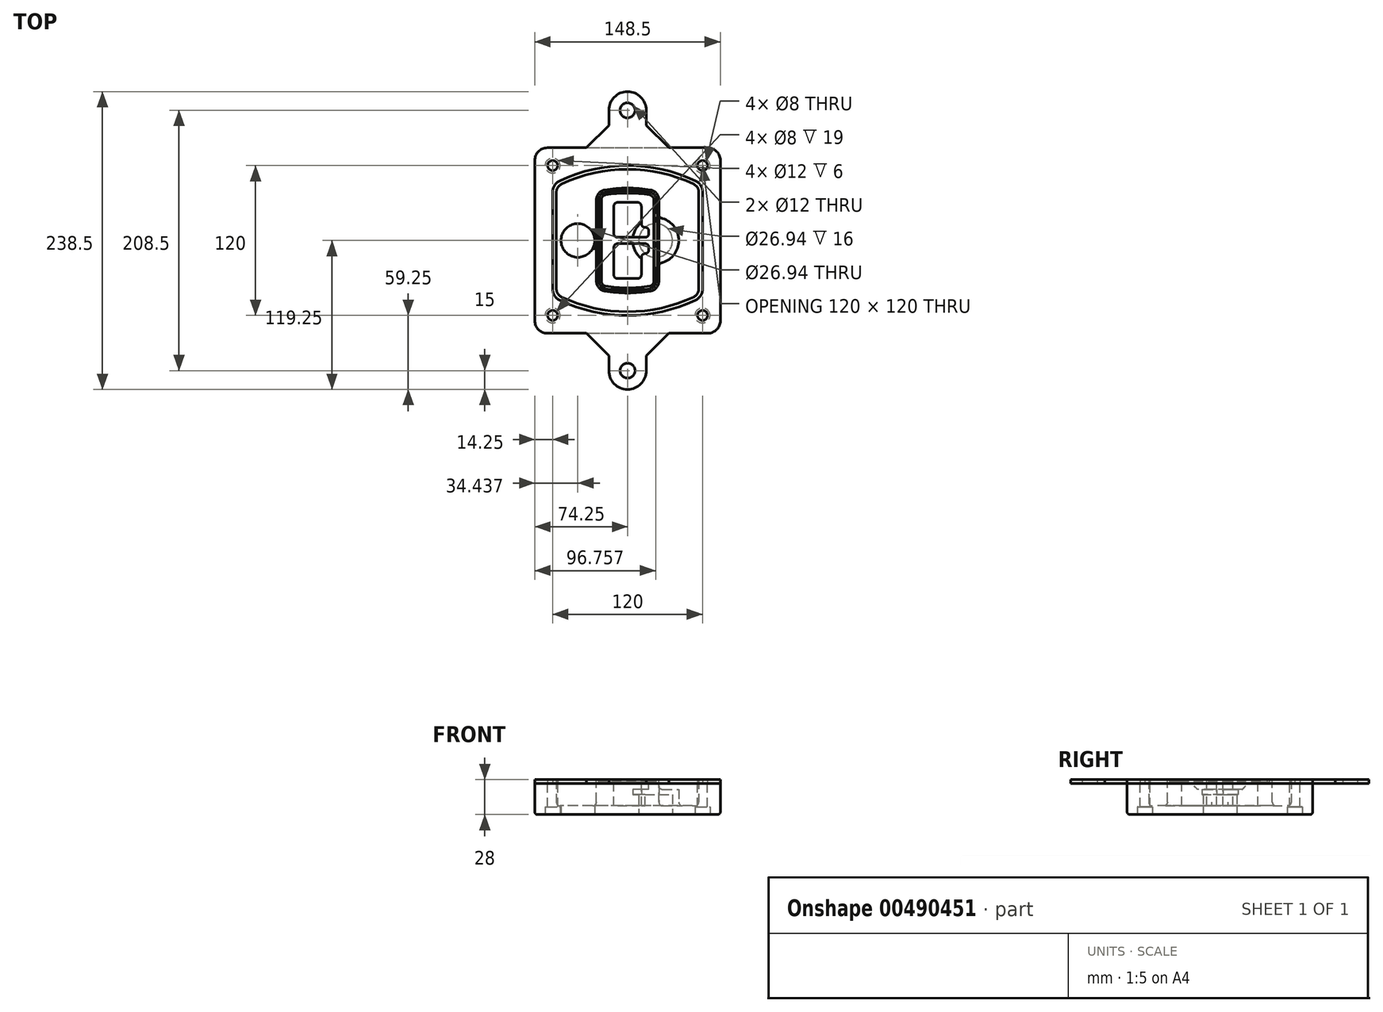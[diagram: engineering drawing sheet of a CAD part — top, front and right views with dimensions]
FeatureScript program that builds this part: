
annotation { "Feature Type Name" : "Feature", "Feature Type Description" : "" }
export const myFeature = defineFeature(function(context is Context, id is Id, definition is map)
    precondition{}
    {
        {
            var Q0;
            Q0=qCreatedBy(makeId("Top.planeOp"),FACE);
            var sketch = newSketch(context, id + "F0", { "sketchPlane" : qUnion([Q0])});
            skPoint(sketch, "E0.rect.middle", {"position": v(0, 0) * mm});
            skLineSegment(sketch, "E1.bottom", {"start": v(-64.25, -74.25) * mm, "end": v(64.25, -74.25) * mm});
            skLineSegment(sketch, "E1.top", {"start": v(-64.25, 74.25) * mm, "end": v(64.25, 74.25) * mm});
            skLineSegment(sketch, "E1.left", {"start": v(-74.25, -64.25) * mm, "end": v(-74.25, 64.25) * mm});
            skLineSegment(sketch, "E1.right", {"start": v(74.25, -64.25) * mm, "end": v(74.25, 64.25) * mm});
            skLineSegment(sketch, "E2", {"start": v(-74.25, 74.25) * mm, "end": v(74.25, -74.25) * mm, "construction": true});
            skLineSegment(sketch, "E3", {"start": v(74.25, 74.25) * mm, "end": v(-74.25, -74.25) * mm, "construction": true});
            skCircle(sketch, "E4", {"center": v(-60, 60) * mm, "radius": 4 * mm});
            skCircle(sketch, "E5", {"center": v(60, 60) * mm, "radius": 4 * mm});
            skCircle(sketch, "E6", {"center": v(60, -60) * mm, "radius": 4 * mm});
            skCircle(sketch, "E7", {"center": v(-60, -60) * mm, "radius": 4 * mm});
            skLineSegment(sketch, "E8", {"start": v(-60, 60) * mm, "end": v(60, 60) * mm, "construction": true});
            skLineSegment(sketch, "E9", {"start": v(60, 60) * mm, "end": v(60, -60) * mm, "construction": true});
            skLineSegment(sketch, "E10", {"start": v(60, -60) * mm, "end": v(-60, -60) * mm, "construction": true});
            skLineSegment(sketch, "E11", {"start": v(-60, -60) * mm, "end": v(-60, 60) * mm, "construction": true});
            skLineSegment(sketch, "E12", {"start": v(-60, 38.83) * mm, "end": v(-60, -38.83) * mm});
            skLineSegment(sketch, "E13", {"start": v(60, 38.83) * mm, "end": v(60, -38.83) * mm});
            skArc(sketch, "E14", {"start": v(54.26, 47.88) * mm, "mid": v(0, 60) * mm, "end": v(-54.26, 47.88) * mm});
            skArc(sketch, "E15", {"start": v(-54.26, -47.88) * mm, "mid": v(0, -60) * mm, "end": v(54.26, -47.88) * mm});
            skLineSegment(sketch, "E16", {"start": v(-60, 0) * mm, "end": v(60, 0) * mm, "construction": true});
            skPoint(sketch, "E17.visualSharp", {"position": v(-60, -45) * mm});
            skArc(sketch, "E17.filletArc", {"start": v(-60, -38.83) * mm, "mid": v(-58.44, -44.2) * mm, "end": v(-54.26, -47.88) * mm});
            skPoint(sketch, "E18.visualSharp", {"position": v(-60, 45) * mm});
            skArc(sketch, "E18.filletArc", {"start": v(-54.26, 47.88) * mm, "mid": v(-58.44, 44.2) * mm, "end": v(-60, 38.83) * mm});
            skPoint(sketch, "E19.visualSharp", {"position": v(60, 45) * mm});
            skArc(sketch, "E19.filletArc", {"start": v(60, 38.83) * mm, "mid": v(58.44, 44.2) * mm, "end": v(54.26, 47.88) * mm});
            skPoint(sketch, "E20.visualSharp", {"position": v(60, -45) * mm});
            skArc(sketch, "E20.filletArc", {"start": v(54.26, -47.88) * mm, "mid": v(58.44, -44.2) * mm, "end": v(60, -38.83) * mm});
            skPoint(sketch, "E21.visualSharp", {"position": v(-74.25, 74.25) * mm});
            skArc(sketch, "E21.filletArc", {"start": v(-64.25, 74.25) * mm, "mid": v(-71.32, 71.32) * mm, "end": v(-74.25, 64.25) * mm});
            skPoint(sketch, "E22.visualSharp", {"position": v(74.25, 74.25) * mm});
            skArc(sketch, "E22.filletArc", {"start": v(74.25, 64.25) * mm, "mid": v(71.32, 71.32) * mm, "end": v(64.25, 74.25) * mm});
            skPoint(sketch, "E23.visualSharp", {"position": v(74.25, -74.25) * mm});
            skArc(sketch, "E23.filletArc", {"start": v(64.25, -74.25) * mm, "mid": v(71.32, -71.32) * mm, "end": v(74.25, -64.25) * mm});
            skPoint(sketch, "E24.visualSharp", {"position": v(-74.25, -74.25) * mm});
            skArc(sketch, "E24.filletArc", {"start": v(-74.25, -64.25) * mm, "mid": v(-71.32, -71.32) * mm, "end": v(-64.25, -74.25) * mm});
            skArc(sketch, "E25.0", {"start": v(57, 38.83) * mm, "mid": v(55.9, 42.58) * mm, "end": v(52.98, 45.17) * mm});
            skLineSegment(sketch, "E25.1", {"start": v(57, 38.83) * mm, "end": v(57, -38.83) * mm});
            skArc(sketch, "E25.2", {"start": v(52.98, -45.17) * mm, "mid": v(55.9, -42.58) * mm, "end": v(57, -38.83) * mm});
            skArc(sketch, "E25.3", {"start": v(-52.98, -45.17) * mm, "mid": v(0, -57) * mm, "end": v(52.98, -45.17) * mm});
            skArc(sketch, "E25.4", {"start": v(-57, -38.83) * mm, "mid": v(-55.9, -42.58) * mm, "end": v(-52.98, -45.17) * mm});
            skArc(sketch, "E25.5", {"start": v(52.98, 45.17) * mm, "mid": v(0, 57) * mm, "end": v(-52.98, 45.17) * mm});
            skLineSegment(sketch, "E25.6", {"start": v(-57, 38.83) * mm, "end": v(-57, -38.83) * mm});
            skArc(sketch, "E25.7", {"start": v(-52.98, 45.17) * mm, "mid": v(-55.9, 42.58) * mm, "end": v(-57, 38.83) * mm});
            skArc(sketch, "E26.0", {"start": v(-55.96, 51.5) * mm, "mid": v(-61.82, 46.33) * mm, "end": v(-64, 38.83) * mm});
            skArc(sketch, "E26.1", {"start": v(55.96, 51.5) * mm, "mid": v(0, 64) * mm, "end": v(-55.96, 51.5) * mm});
            skArc(sketch, "E26.2", {"start": v(64, 38.83) * mm, "mid": v(61.82, 46.33) * mm, "end": v(55.96, 51.5) * mm});
            skLineSegment(sketch, "E26.3", {"start": v(64, 38.83) * mm, "end": v(64, -38.83) * mm});
            skArc(sketch, "E26.4", {"start": v(55.96, -51.5) * mm, "mid": v(61.82, -46.33) * mm, "end": v(64, -38.83) * mm});
            skLineSegment(sketch, "E26.5", {"start": v(-64, 38.83) * mm, "end": v(-64, -38.83) * mm});
            skArc(sketch, "E26.6", {"start": v(-55.96, -51.5) * mm, "mid": v(0, -64) * mm, "end": v(55.96, -51.5) * mm});
            skArc(sketch, "E26.7", {"start": v(-64, -38.83) * mm, "mid": v(-61.82, -46.33) * mm, "end": v(-55.96, -51.5) * mm});
            skSolve(sketch);
        }
        {
            var Q0;
            Q0=makeQuery(id+"F0.imprint","IMPRINT",FACE,{"disambiguationData":[TD([[makeQuery(id+"F0.imprint","IMPRINT",EDGE,{"derivedFrom":sQuery(id+"F0.wireOp",EDGE,"E1.bottom")}),1.0]])]});
            var Q1;
            Q1=makeQuery(id+"F0.imprint","IMPRINT",FACE,{"disambiguationData":[TD([[makeQuery(id+"F0.imprint","IMPRINT",EDGE,{"derivedFrom":sQuery(id+"F0.wireOp",EDGE,"E12")}),1.0]])]});
            var Q2;
            Q2=makeQuery(id+"F0.imprint","IMPRINT",FACE,{"disambiguationData":[TD([[makeQuery(id+"F0.imprint","IMPRINT",EDGE,{"derivedFrom":sQuery(id+"F0.wireOp",EDGE,"E25.0")}),1.0]])]});
            var Q3;
            Q3=makeQuery(id+"F0.imprint","IMPRINT",FACE,{"disambiguationData":[TD([[makeQuery(id+"F0.imprint","IMPRINT",EDGE,{"derivedFrom":sQuery(id+"F0.wireOp",EDGE,"E12")}),-1.0]])]});
            extrude(context, id + "F1", {"entities" : qUnion([Q0, Q1, Q2, Q3]), "oppositeDirection" : true, "depth" : 25 * mm});
        }
        {
            var Q0;
            Q0=makeQuery(id+"F0.imprint","IMPRINT",FACE,{"disambiguationData":[TD([[makeQuery(id+"F0.imprint","IMPRINT",EDGE,{"derivedFrom":sQuery(id+"F0.wireOp",EDGE,"E12")}),1.0]])]});
            extrude(context, id + "F2", {"entities" : qUnion([Q0]), "operationType" : NewBodyOperationType.ADD, "depth" : 3 * mm});
        }
        {
            var Q0;
            Q0=makeQuery(id+"F0.imprint","IMPRINT",FACE,{"disambiguationData":[TD([[makeQuery(id+"F0.imprint","IMPRINT",EDGE,{"derivedFrom":sQuery(id+"F0.wireOp",EDGE,"E25.0")}),1.0]])]});
            extrude(context, id + "F3", {"entities" : qUnion([Q0]), "operationType" : NewBodyOperationType.REMOVE, "oppositeDirection" : true, "depth" : 18 * mm});
        }
        {
            var Q0;
            Q0=makeQuery(id+"F2.opExtrude","CAP_FACE",FACE,{"disambiguationData":[OSD([sQuery(id+"F0.wireOp",EDGE,"E12"),sQuery(id+"F0.wireOp",EDGE,"E13"),sQuery(id+"F0.wireOp",EDGE,"E14"),sQuery(id+"F0.wireOp",EDGE,"E15"),sQuery(id+"F0.wireOp",EDGE,"E17.filletArc"),sQuery(id+"F0.wireOp",EDGE,"E18.filletArc"),sQuery(id+"F0.wireOp",EDGE,"E19.filletArc"),sQuery(id+"F0.wireOp",EDGE,"E20.filletArc"),sQuery(id+"F0.wireOp",EDGE,"E25.0"),sQuery(id+"F0.wireOp",EDGE,"E25.1"),sQuery(id+"F0.wireOp",EDGE,"E25.2"),sQuery(id+"F0.wireOp",EDGE,"E25.3"),sQuery(id+"F0.wireOp",EDGE,"E25.4"),sQuery(id+"F0.wireOp",EDGE,"E25.5"),sQuery(id+"F0.wireOp",EDGE,"E25.6"),sQuery(id+"F0.wireOp",EDGE,"E25.7")])],"isStart":false});
            var sketch = newSketch(context, id + "F4", { "sketchPlane" : qUnion([Q0])});
            skArc(sketch, "E27.0", {"start": v(-18.34, -40.45) * mm, "mid": v(0, -42) * mm, "end": v(18.34, -40.45) * mm});
            skArc(sketch, "E28.0", {"start": v(18.34, 40.45) * mm, "mid": v(0, 42) * mm, "end": v(-18.34, 40.45) * mm});
            skLineSegment(sketch, "E29", {"start": v(-25, 32.57) * mm, "end": v(-25, -32.57) * mm});
            skLineSegment(sketch, "E30", {"start": v(25, 32.57) * mm, "end": v(25, -32.57) * mm});
            skLineSegment(sketch, "E31", {"start": v(-25, 39.1) * mm, "end": v(25, 39.1) * mm, "construction": true});
            skLineSegment(sketch, "E32", {"start": v(-25, -39.1) * mm, "end": v(25, -39.1) * mm, "construction": true});
            skPoint(sketch, "E33.visualSharp", {"position": v(-25, 39.1) * mm});
            skArc(sketch, "E33.filletArc", {"start": v(-18.34, 40.45) * mm, "mid": v(-23.11, 37.73) * mm, "end": v(-25, 32.57) * mm});
            skPoint(sketch, "E34.visualSharp", {"position": v(25, 39.1) * mm});
            skArc(sketch, "E34.filletArc", {"start": v(25, 32.57) * mm, "mid": v(23.11, 37.73) * mm, "end": v(18.34, 40.45) * mm});
            skPoint(sketch, "E35.visualSharp", {"position": v(25, -39.1) * mm});
            skArc(sketch, "E35.filletArc", {"start": v(18.34, -40.45) * mm, "mid": v(23.11, -37.73) * mm, "end": v(25, -32.57) * mm});
            skPoint(sketch, "E36.visualSharp", {"position": v(-25, -39.1) * mm});
            skArc(sketch, "E36.filletArc", {"start": v(-25, -32.57) * mm, "mid": v(-23.11, -37.73) * mm, "end": v(-18.34, -40.45) * mm});
            skArc(sketch, "E37.0", {"start": v(52.98, 45.17) * mm, "mid": v(0, 57) * mm, "end": v(-52.98, 45.17) * mm});
            skArc(sketch, "E37.1", {"start": v(-52.98, 45.17) * mm, "mid": v(-55.9, 42.58) * mm, "end": v(-57, 38.83) * mm});
            skLineSegment(sketch, "E37.2", {"start": v(-57, 38.83) * mm, "end": v(-57, -38.83) * mm});
            skArc(sketch, "E37.3", {"start": v(-57, -38.83) * mm, "mid": v(-55.9, -42.58) * mm, "end": v(-52.98, -45.17) * mm});
            skArc(sketch, "E37.4", {"start": v(-52.98, -45.17) * mm, "mid": v(0, -57) * mm, "end": v(52.98, -45.17) * mm});
            skArc(sketch, "E37.5", {"start": v(52.98, -45.17) * mm, "mid": v(55.9, -42.58) * mm, "end": v(57, -38.83) * mm});
            skLineSegment(sketch, "E37.6", {"start": v(57, 38.83) * mm, "end": v(57, -38.83) * mm});
            skArc(sketch, "E37.7", {"start": v(57, 38.83) * mm, "mid": v(55.9, 42.58) * mm, "end": v(52.98, 45.17) * mm});
            skLineSegment(sketch, "E38.0", {"start": v(23, 32.57) * mm, "end": v(23, -32.57) * mm});
            skArc(sketch, "E38.1", {"start": v(18, -38.48) * mm, "mid": v(21.58, -36.44) * mm, "end": v(23, -32.57) * mm});
            skArc(sketch, "E38.2", {"start": v(-18, -38.48) * mm, "mid": v(0, -40) * mm, "end": v(18, -38.48) * mm});
            skArc(sketch, "E38.3", {"start": v(-23, -32.57) * mm, "mid": v(-21.58, -36.44) * mm, "end": v(-18, -38.48) * mm});
            skLineSegment(sketch, "E38.4", {"start": v(-23, 32.57) * mm, "end": v(-23, -32.57) * mm});
            skArc(sketch, "E38.5", {"start": v(23, 32.57) * mm, "mid": v(21.58, 36.44) * mm, "end": v(18, 38.48) * mm});
            skArc(sketch, "E38.6", {"start": v(-18, 38.48) * mm, "mid": v(-21.58, 36.44) * mm, "end": v(-23, 32.57) * mm});
            skArc(sketch, "E38.7", {"start": v(18, 38.48) * mm, "mid": v(0, 40) * mm, "end": v(-18, 38.48) * mm});
            skArc(sketch, "E39.0", {"start": v(21, 32.57) * mm, "mid": v(20.06, 35.15) * mm, "end": v(17.67, 36.5) * mm});
            skLineSegment(sketch, "E39.1", {"start": v(21, 32.57) * mm, "end": v(21, -32.57) * mm});
            skArc(sketch, "E39.2", {"start": v(17.67, -36.5) * mm, "mid": v(20.06, -35.15) * mm, "end": v(21, -32.57) * mm});
            skArc(sketch, "E39.3", {"start": v(-17.67, -36.5) * mm, "mid": v(0, -38) * mm, "end": v(17.67, -36.5) * mm});
            skArc(sketch, "E39.4", {"start": v(-21, -32.57) * mm, "mid": v(-20.06, -35.15) * mm, "end": v(-17.67, -36.5) * mm});
            skArc(sketch, "E39.5", {"start": v(17.67, 36.5) * mm, "mid": v(0, 38) * mm, "end": v(-17.67, 36.5) * mm});
            skLineSegment(sketch, "E39.6", {"start": v(-21, 32.57) * mm, "end": v(-21, -32.57) * mm});
            skArc(sketch, "E39.7", {"start": v(-17.67, 36.5) * mm, "mid": v(-20.06, 35.15) * mm, "end": v(-21, 32.57) * mm});
            skLineSegment(sketch, "E40", {"start": v(-25, 0) * mm, "end": v(25, 0) * mm, "construction": true});
            skLineSegment(sketch, "E41", {"start": v(-11, 5.5) * mm, "end": v(-11, 27.5) * mm});
            skLineSegment(sketch, "E42", {"start": v(-8, 30.5) * mm, "end": v(8, 30.5) * mm});
            skLineSegment(sketch, "E43", {"start": v(11, 27.5) * mm, "end": v(11, 13.5) * mm});
            skLineSegment(sketch, "E44", {"start": v(14, 10.5) * mm, "end": v(14, 10.5) * mm});
            skLineSegment(sketch, "E45", {"start": v(17, 7.5) * mm, "end": v(17, 5.5) * mm});
            skLineSegment(sketch, "E46", {"start": v(14, 2.5) * mm, "end": v(-8, 2.5) * mm});
            skPoint(sketch, "E47.visualSharp", {"position": v(-11, 30.5) * mm});
            skArc(sketch, "E47.filletArc", {"start": v(-8, 30.5) * mm, "mid": v(-10.12, 29.62) * mm, "end": v(-11, 27.5) * mm});
            skPoint(sketch, "E48.visualSharp", {"position": v(11, 30.5) * mm});
            skArc(sketch, "E48.filletArc", {"start": v(11, 27.5) * mm, "mid": v(10.12, 29.62) * mm, "end": v(8, 30.5) * mm});
            skPoint(sketch, "E49.visualSharp", {"position": v(11, 10.5) * mm});
            skArc(sketch, "E49.filletArc", {"start": v(11, 13.5) * mm, "mid": v(11.88, 11.38) * mm, "end": v(14, 10.5) * mm});
            skPoint(sketch, "E50.visualSharp", {"position": v(17, 10.5) * mm});
            skArc(sketch, "E50.filletArc", {"start": v(17, 7.5) * mm, "mid": v(16.12, 9.62) * mm, "end": v(14, 10.5) * mm});
            skPoint(sketch, "E51.visualSharp", {"position": v(17, 2.5) * mm});
            skArc(sketch, "E51.filletArc", {"start": v(14, 2.5) * mm, "mid": v(16.12, 3.38) * mm, "end": v(17, 5.5) * mm});
            skPoint(sketch, "E52.visualSharp", {"position": v(-11, 2.5) * mm});
            skArc(sketch, "E52.filletArc", {"start": v(-11, 5.5) * mm, "mid": v(-10.12, 3.38) * mm, "end": v(-8, 2.5) * mm});
            skLineSegment(sketch, "E53.0.MirrorCS", {"start": v(14, -2.5) * mm, "end": v(-8, -2.5) * mm});
            skArc(sketch, "E54.0.MirrorCS", {"start": v(-11, -5.5) * mm, "mid": v(-10.12, -3.38) * mm, "end": v(-8, -2.5) * mm});
            skLineSegment(sketch, "E55.0.MirrorCS", {"start": v(-11, -5.5) * mm, "end": v(-11, -27.5) * mm});
            skArc(sketch, "E56.0.MirrorCS", {"start": v(-8, -30.5) * mm, "mid": v(-10.12, -29.62) * mm, "end": v(-11, -27.5) * mm});
            skLineSegment(sketch, "E57.0.MirrorCS", {"start": v(-8, -30.5) * mm, "end": v(8, -30.5) * mm});
            skArc(sketch, "E58.0.MirrorCS", {"start": v(11, -27.5) * mm, "mid": v(10.12, -29.62) * mm, "end": v(8, -30.5) * mm});
            skLineSegment(sketch, "E59.0.MirrorCS", {"start": v(11, -27.5) * mm, "end": v(11, -13.5) * mm});
            skArc(sketch, "E60.0.MirrorCS", {"start": v(11, -13.5) * mm, "mid": v(11.88, -11.38) * mm, "end": v(14, -10.5) * mm});
            skArc(sketch, "E61.0.MirrorCS", {"start": v(17, -7.5) * mm, "mid": v(16.12, -9.62) * mm, "end": v(14, -10.5) * mm});
            skLineSegment(sketch, "E62.0.MirrorCS", {"start": v(17, -7.5) * mm, "end": v(17, -5.5) * mm});
            skArc(sketch, "E63.0.MirrorCS", {"start": v(14, -2.5) * mm, "mid": v(16.12, -3.38) * mm, "end": v(17, -5.5) * mm});
            skSolve(sketch);
        }
        {
            var Q0;
            Q0=makeQuery(id+"F4.imprint","IMPRINT",FACE,{"disambiguationData":[TD([[makeQuery(id+"F4.imprint","IMPRINT",EDGE,{"derivedFrom":sQuery(id+"F4.wireOp",EDGE,"E27.0")}),1.0]])]});
            var Q1;
            Q1=makeQuery(id+"F4.imprint","IMPRINT",FACE,{"disambiguationData":[TD([[makeQuery(id+"F4.imprint","IMPRINT",EDGE,{"derivedFrom":sQuery(id+"F4.wireOp",EDGE,"E38.0")}),-1.0]])]});
            var Q2;
            Q2=makeQuery(id+"F4.imprint","IMPRINT",FACE,{"disambiguationData":[TD([[makeQuery(id+"F4.imprint","IMPRINT",EDGE,{"derivedFrom":sQuery(id+"F4.wireOp",EDGE,"E39.0")}),1.0]])]});
            extrude(context, id + "F5", {"entities" : qUnion([Q0, Q1, Q2]), "operationType" : NewBodyOperationType.ADD, "endBound" : BoundingType.UP_TO_NEXT, "oppositeDirection" : true, "depth" : 25 * mm});
        }
        {
            var Q0;
            Q0=makeQuery(id+"F4.imprint","IMPRINT",FACE,{"disambiguationData":[TD([[makeQuery(id+"F4.imprint","IMPRINT",EDGE,{"derivedFrom":sQuery(id+"F4.wireOp",EDGE,"E38.0")}),-1.0]])]});
            extrude(context, id + "F6", {"entities" : qUnion([Q0]), "operationType" : NewBodyOperationType.REMOVE, "oppositeDirection" : true, "depth" : 2 * mm});
        }
        {
            var Q0;
            Q0=makeQuery(id+"F1.opExtrude","CAP_FACE",FACE,{"disambiguationData":[OSD([sQuery(id+"F0.wireOp",EDGE,"E1.bottom"),sQuery(id+"F0.wireOp",EDGE,"E1.top"),sQuery(id+"F0.wireOp",EDGE,"E1.left"),sQuery(id+"F0.wireOp",EDGE,"E1.right"),sQuery(id+"F0.wireOp",EDGE,"E4"),sQuery(id+"F0.wireOp",EDGE,"E5"),sQuery(id+"F0.wireOp",EDGE,"E6"),sQuery(id+"F0.wireOp",EDGE,"E7"),sQuery(id+"F0.wireOp",EDGE,"E21.filletArc"),sQuery(id+"F0.wireOp",EDGE,"E22.filletArc"),sQuery(id+"F0.wireOp",EDGE,"E23.filletArc"),sQuery(id+"F0.wireOp",EDGE,"E24.filletArc")])],"isStart":false});
            var sketch = newSketch(context, id + "F7", { "sketchPlane" : qUnion([Q0])});
            skCircle(sketch, "E64", {"center": v(22.5, 0) * mm, "radius": 13.47 * mm});
            skCircle(sketch, "E65", {"center": v(-39.81, 0) * mm, "radius": 13.47 * mm});
            skLineSegment(sketch, "E66", {"start": v(74.25, 0) * mm, "end": v(-74.25, 0) * mm});
            skCircle(sketch, "E67", {"center": v(22.5, 0) * mm, "radius": 18.47 * mm});
            skCircle(sketch, "E68", {"center": v(60, -60) * mm, "radius": 6 * mm});
            skCircle(sketch, "E69", {"center": v(-60, -60) * mm, "radius": 6 * mm});
            skCircle(sketch, "E70", {"center": v(-60, 60) * mm, "radius": 6 * mm});
            skCircle(sketch, "E71", {"center": v(60, 60) * mm, "radius": 6 * mm});
            skSolve(sketch);
        }
        {
            var Q0;
            {var subQ1=sQuery(id+"F7.wireOp",EDGE,"E66");var subQ4=sQuery(id+"F7.wireOp",EDGE,"E64");var subQ6=makeQuery(id+"F7.imprint","INTERSECT",VERTEX,{"disambiguationData":[OD(0.0)],"derivedFrom":[subQ4,subQ1]});Q0=makeQuery(id+"F7.imprint","IMPRINT",FACE,{"disambiguationData":[TD([[makeQuery(id+"F7.imprint","IMPRINT",EDGE,{"disambiguationData":[TD([[subQ6,-1.0]])],"derivedFrom":subQ4}),-1.0]])]});}
            var Q1;
            {var subQ0=sQuery(id+"F7.wireOp",EDGE,"E66");var subQ1=sQuery(id+"F7.wireOp",EDGE,"E64");var subQ3=makeQuery(id+"F7.imprint","INTERSECT",VERTEX,{"disambiguationData":[OD(0.0)],"derivedFrom":[subQ1,subQ0]});Q1=makeQuery(id+"F7.imprint","IMPRINT",FACE,{"disambiguationData":[TD([[makeQuery(id+"F7.imprint","IMPRINT",EDGE,{"disambiguationData":[TD([[subQ3,-1.0]])],"derivedFrom":subQ1}),1.0]])]});}
            var Q2;
            {var subQ0=sQuery(id+"F7.wireOp",EDGE,"E66");var subQ1=sQuery(id+"F7.wireOp",EDGE,"E64");var subQ3=makeQuery(id+"F7.imprint","INTERSECT",VERTEX,{"disambiguationData":[OD(0.0)],"derivedFrom":[subQ1,subQ0]});Q2=makeQuery(id+"F7.imprint","IMPRINT",FACE,{"disambiguationData":[TD([[makeQuery(id+"F7.imprint","IMPRINT",EDGE,{"disambiguationData":[TD([[subQ3,1.0]])],"derivedFrom":subQ1}),1.0]])]});}
            var Q3;
            {var subQ1=sQuery(id+"F7.wireOp",EDGE,"E66");var subQ4=sQuery(id+"F7.wireOp",EDGE,"E64");var subQ6=makeQuery(id+"F7.imprint","INTERSECT",VERTEX,{"disambiguationData":[OD(0.0)],"derivedFrom":[subQ4,subQ1]});Q3=makeQuery(id+"F7.imprint","IMPRINT",FACE,{"disambiguationData":[TD([[makeQuery(id+"F7.imprint","IMPRINT",EDGE,{"disambiguationData":[TD([[subQ6,1.0]])],"derivedFrom":subQ4}),-1.0]])]});}
            extrude(context, id + "F8", {"entities" : qUnion([Q0, Q1, Q2, Q3]), "operationType" : NewBodyOperationType.ADD, "oppositeDirection" : true, "depth" : 20 * mm});
        }
        {
            var Q0;
            {var subQ0=sQuery(id+"F7.wireOp",EDGE,"E66");var subQ1=sQuery(id+"F7.wireOp",EDGE,"E64");var subQ3=makeQuery(id+"F7.imprint","INTERSECT",VERTEX,{"disambiguationData":[OD(0.0)],"derivedFrom":[subQ1,subQ0]});Q0=makeQuery(id+"F7.imprint","IMPRINT",FACE,{"disambiguationData":[TD([[makeQuery(id+"F7.imprint","IMPRINT",EDGE,{"disambiguationData":[TD([[subQ3,-1.0]])],"derivedFrom":subQ1}),1.0]])]});}
            var Q1;
            {var subQ0=sQuery(id+"F7.wireOp",EDGE,"E66");var subQ1=sQuery(id+"F7.wireOp",EDGE,"E64");var subQ3=makeQuery(id+"F7.imprint","INTERSECT",VERTEX,{"disambiguationData":[OD(0.0)],"derivedFrom":[subQ1,subQ0]});Q1=makeQuery(id+"F7.imprint","IMPRINT",FACE,{"disambiguationData":[TD([[makeQuery(id+"F7.imprint","IMPRINT",EDGE,{"disambiguationData":[TD([[subQ3,1.0]])],"derivedFrom":subQ1}),1.0]])]});}
            extrude(context, id + "F9", {"entities" : qUnion([Q0, Q1]), "operationType" : NewBodyOperationType.REMOVE, "oppositeDirection" : true, "depth" : 16 * mm});
        }
        {
            var Q0;
            {var subQ0=sQuery(id+"F7.wireOp",EDGE,"E66");var subQ1=sQuery(id+"F7.wireOp",EDGE,"E65");var subQ3=makeQuery(id+"F7.imprint","INTERSECT",VERTEX,{"disambiguationData":[OD(0.0)],"derivedFrom":[subQ1,subQ0]});Q0=makeQuery(id+"F7.imprint","IMPRINT",FACE,{"disambiguationData":[TD([[makeQuery(id+"F7.imprint","IMPRINT",EDGE,{"disambiguationData":[TD([[subQ3,-1.0]])],"derivedFrom":subQ1}),1.0]])]});}
            var Q1;
            {var subQ0=sQuery(id+"F7.wireOp",EDGE,"E66");var subQ1=sQuery(id+"F7.wireOp",EDGE,"E65");var subQ3=makeQuery(id+"F7.imprint","INTERSECT",VERTEX,{"disambiguationData":[OD(0.0)],"derivedFrom":[subQ1,subQ0]});Q1=makeQuery(id+"F7.imprint","IMPRINT",FACE,{"disambiguationData":[TD([[makeQuery(id+"F7.imprint","IMPRINT",EDGE,{"disambiguationData":[TD([[subQ3,1.0]])],"derivedFrom":subQ1}),1.0]])]});}
            extrude(context, id + "F10", {"entities" : qUnion([Q0, Q1]), "operationType" : NewBodyOperationType.REMOVE, "oppositeDirection" : true, "depth" : 25 * mm});
        }
        {
            var Q0;
            Q0=makeQuery(id+"F7.imprint","IMPRINT",FACE,{"disambiguationData":[TD([[makeQuery(id+"F7.imprint","IMPRINT",EDGE,{"derivedFrom":sQuery(id+"F7.wireOp",EDGE,"E68")}),1.0]])]});
            var Q1;
            Q1=makeQuery(id+"F7.imprint","IMPRINT",FACE,{"disambiguationData":[TD([[makeQuery(id+"F7.imprint","IMPRINT",EDGE,{"derivedFrom":makeQuery(id+"F1.opExtrude","CAP_EDGE",EDGE,{"disambiguationData":[OSD([sQuery(id+"F0.wireOp",EDGE,"E5")])],"isStart":false})}),-1.0]])]});
            var Q2;
            Q2=makeQuery(id+"F7.imprint","IMPRINT",FACE,{"disambiguationData":[TD([[makeQuery(id+"F7.imprint","IMPRINT",EDGE,{"derivedFrom":sQuery(id+"F7.wireOp",EDGE,"E69")}),1.0]])]});
            var Q3;
            Q3=makeQuery(id+"F7.imprint","IMPRINT",FACE,{"disambiguationData":[TD([[makeQuery(id+"F7.imprint","IMPRINT",EDGE,{"derivedFrom":makeQuery(id+"F1.opExtrude","CAP_EDGE",EDGE,{"disambiguationData":[OSD([sQuery(id+"F0.wireOp",EDGE,"E4")])],"isStart":false})}),-1.0]])]});
            var Q4;
            Q4=makeQuery(id+"F7.imprint","IMPRINT",FACE,{"disambiguationData":[TD([[makeQuery(id+"F7.imprint","IMPRINT",EDGE,{"derivedFrom":sQuery(id+"F7.wireOp",EDGE,"E70")}),1.0]])]});
            var Q5;
            Q5=makeQuery(id+"F7.imprint","IMPRINT",FACE,{"disambiguationData":[TD([[makeQuery(id+"F7.imprint","IMPRINT",EDGE,{"derivedFrom":makeQuery(id+"F1.opExtrude","CAP_EDGE",EDGE,{"disambiguationData":[OSD([sQuery(id+"F0.wireOp",EDGE,"E7")])],"isStart":false})}),-1.0]])]});
            var Q6;
            Q6=makeQuery(id+"F7.imprint","IMPRINT",FACE,{"disambiguationData":[TD([[makeQuery(id+"F7.imprint","IMPRINT",EDGE,{"derivedFrom":sQuery(id+"F7.wireOp",EDGE,"E71")}),1.0]])]});
            var Q7;
            Q7=makeQuery(id+"F7.imprint","IMPRINT",FACE,{"disambiguationData":[TD([[makeQuery(id+"F7.imprint","IMPRINT",EDGE,{"derivedFrom":makeQuery(id+"F1.opExtrude","CAP_EDGE",EDGE,{"disambiguationData":[OSD([sQuery(id+"F0.wireOp",EDGE,"E6")])],"isStart":false})}),-1.0]])]});
            extrude(context, id + "F11", {"entities" : qUnion([Q0, Q1, Q2, Q3, Q4, Q5, Q6, Q7]), "operationType" : NewBodyOperationType.REMOVE, "oppositeDirection" : true, "depth" : 6 * mm});
        }
        {
            var Q0;
            Q0=makeQuery(id+"F9.boolean.opBoolean","COPY",FACE,{"derivedFrom":makeQuery(id+"F9.opExtrude","CAP_FACE",FACE,{"disambiguationData":[OSD([sQuery(id+"F7.wireOp",EDGE,"E64")])],"isStart":false})});
            var sketch = newSketch(context, id + "F12", { "sketchPlane" : qUnion([Q0])});
            skArc(sketch, "E72.0", {"start": v(11, 14.45) * mm, "mid": v(6.45, 9.13) * mm, "end": v(4.2, 2.5) * mm});
            skArc(sketch, "E72.1", {"start": v(4.2, -2.5) * mm, "mid": v(6.45, -9.13) * mm, "end": v(11, -14.45) * mm});
            skLineSegment(sketch, "E73", {"start": v(4.2, -2.5) * mm, "end": v(14, -2.5) * mm});
            skLineSegment(sketch, "E74.0", {"start": v(14, 2.5) * mm, "end": v(4.2, 2.5) * mm});
            skArc(sketch, "E74.1", {"start": v(14, 2.5) * mm, "mid": v(16.12, 3.38) * mm, "end": v(17, 5.5) * mm});
            skLineSegment(sketch, "E74.2", {"start": v(17, 7.5) * mm, "end": v(17, 5.5) * mm});
            skArc(sketch, "E74.3", {"start": v(17, 7.5) * mm, "mid": v(16.12, 9.62) * mm, "end": v(14, 10.5) * mm});
            skArc(sketch, "E74.4", {"start": v(11, 13.5) * mm, "mid": v(11.88, 11.38) * mm, "end": v(14, 10.5) * mm});
            skLineSegment(sketch, "E74.5", {"start": v(11, 14.45) * mm, "end": v(11, 13.5) * mm});
            skLineSegment(sketch, "E74.7", {"start": v(14, -2.5) * mm, "end": v(4.2, -2.5) * mm});
            skArc(sketch, "E74.8", {"start": v(14, -2.5) * mm, "mid": v(16.12, -3.38) * mm, "end": v(17, -5.5) * mm});
            skLineSegment(sketch, "E74.9", {"start": v(17, -7.5) * mm, "end": v(17, -5.5) * mm});
            skArc(sketch, "E74.10", {"start": v(17, -7.5) * mm, "mid": v(16.12, -9.62) * mm, "end": v(14, -10.5) * mm});
            skArc(sketch, "E74.11", {"start": v(11, -13.5) * mm, "mid": v(11.88, -11.38) * mm, "end": v(14, -10.5) * mm});
            skLineSegment(sketch, "E74.12", {"start": v(11, -14.45) * mm, "end": v(11, -13.5) * mm});
            skPoint(sketch, "E75.orphan", {"position": v(11, -27.5) * mm});
            skPoint(sketch, "E76.orphan", {"position": v(-8, -2.5) * mm});
            skPoint(sketch, "E77.orphan", {"position": v(-8, 2.5) * mm});
            skPoint(sketch, "E78.orphan", {"position": v(11, 27.5) * mm});
            skSolve(sketch);
        }
        {
            var Q0;
            {var subQ7=sQuery(id+"F12.wireOp",EDGE,"E72.0");var subQ14=sQuery(id+"F12.wireOp",EDGE,"E72.1");var subQ16=sQuery(id+"F12.wireOp",EDGE,"E74.1");var subQ18=sQuery(id+"F12.wireOp",EDGE,"E74.8");Q0=qUnion([makeQuery(id+"F12.imprint","IMPRINT",FACE,{"disambiguationData":[TD([[makeQuery(id+"F12.imprint","IMPRINT",EDGE,{"derivedFrom":subQ7}),1.0]])]}),makeQuery(id+"F12.imprint","IMPRINT",FACE,{"disambiguationData":[TD([[makeQuery(id+"F12.imprint","IMPRINT",EDGE,{"derivedFrom":subQ14}),1.0]])]}),makeQuery(id+"F12.imprint","IMPRINT",FACE,{"disambiguationData":[TD([[makeQuery(id+"F12.imprint","IMPRINT",EDGE,{"derivedFrom":subQ16}),1.0]])]}),makeQuery(id+"F12.imprint","IMPRINT",FACE,{"disambiguationData":[TD([[makeQuery(id+"F12.imprint","IMPRINT",EDGE,{"derivedFrom":subQ18}),-1.0]])]})]);}
            var Q1;
            Q1=makeQuery(id+"F5.boolean.opBoolean","SPLIT",FACE,{"disambiguationData":[TD([makeQuery(id+"F5.opExtrude","SWEPT_FACE",FACE,{"disambiguationData":[OSD([sQuery(id+"F4.wireOp",EDGE,"E41")])]})])],"derivedFrom":makeQuery(id+"F3.boolean.opBoolean","COPY",FACE,{"derivedFrom":makeQuery(id+"F3.opExtrude","CAP_FACE",FACE,{"disambiguationData":[OSD([sQuery(id+"F0.wireOp",EDGE,"E25.0"),sQuery(id+"F0.wireOp",EDGE,"E25.1"),sQuery(id+"F0.wireOp",EDGE,"E25.2"),sQuery(id+"F0.wireOp",EDGE,"E25.3"),sQuery(id+"F0.wireOp",EDGE,"E25.4"),sQuery(id+"F0.wireOp",EDGE,"E25.5"),sQuery(id+"F0.wireOp",EDGE,"E25.6"),sQuery(id+"F0.wireOp",EDGE,"E25.7")])],"isStart":false})})});
            extrude(context, id + "F13", {"entities" : qUnion([Q0]), "operationType" : NewBodyOperationType.REMOVE, "endBound" : BoundingType.UP_TO_SURFACE, "endBoundEntityFace" : qUnion([Q1]), "depth" : 25 * mm});
        }
        {
            var Q0;
            Q0=makeQuery(id+"F3.boolean.opBoolean","COPY",EDGE,{"derivedFrom":makeQuery(id+"F3.opExtrude","CAP_EDGE",EDGE,{"disambiguationData":[OSD([sQuery(id+"F0.wireOp",EDGE,"E25.6")])],"isStart":false})});
            var Q1;
            Q1=makeQuery(id+"F8.boolean.opBoolean","INTERSECT",EDGE,{"derivedFrom":[makeQuery(id+"F5.opExtrude","SWEPT_FACE",FACE,{"disambiguationData":[OSD([sQuery(id+"F4.wireOp",EDGE,"E30")])]}),makeQuery(id+"F8.opExtrude","CAP_FACE",FACE,{"disambiguationData":[OSD([sQuery(id+"F7.wireOp",EDGE,"E67")])],"isStart":false})]});
            var Q2;
            Q2=makeQuery(id+"F8.boolean.opBoolean","INTERSECT",EDGE,{"disambiguationData":[OD(1.0)],"derivedFrom":[makeQuery(id+"F5.opExtrude","SWEPT_FACE",FACE,{"disambiguationData":[OSD([sQuery(id+"F4.wireOp",EDGE,"E30")])]}),makeQuery(id+"F8.opExtrude","SWEPT_FACE",FACE,{"disambiguationData":[OSD([sQuery(id+"F7.wireOp",EDGE,"E67")])]})]});
            var Q3;
            {var subQ0=sQuery(id+"F4.wireOp",EDGE,"E30");Q3=makeQuery(id+"F8.boolean.opBoolean","SPLIT",EDGE,{"disambiguationData":[TD([makeQuery(id+"F5.opExtrude","SWEPT_FACE",FACE,{"disambiguationData":[OSD([sQuery(id+"F4.wireOp",EDGE,"E35.filletArc")])]})])],"derivedFrom":makeQuery(id+"F5.opExtrude","CAP_EDGE",EDGE,{"disambiguationData":[OSD([subQ0])],"isStart":false})});}
            var Q4;
            {var subQ0=sQuery(id+"F0.wireOp",EDGE,"E25.7");var subQ1=sQuery(id+"F0.wireOp",EDGE,"E25.1");var subQ2=sQuery(id+"F0.wireOp",EDGE,"E25.6");var subQ3=sQuery(id+"F0.wireOp",EDGE,"E25.5");var subQ4=sQuery(id+"F0.wireOp",EDGE,"E25.4");var subQ5=sQuery(id+"F0.wireOp",EDGE,"E25.0");var subQ6=sQuery(id+"F0.wireOp",EDGE,"E25.2");var subQ7=sQuery(id+"F0.wireOp",EDGE,"E25.3");Q4=makeQuery(id+"F8.boolean.opBoolean","INTERSECT",EDGE,{"derivedFrom":[makeQuery(id+"F5.boolean.opBoolean","SPLIT",FACE,{"disambiguationData":[TD([makeQuery(id+"F2.opExtrude","SWEPT_FACE",FACE,{"disambiguationData":[OSD([subQ5])]})])],"derivedFrom":makeQuery(id+"F3.boolean.opBoolean","COPY",FACE,{"derivedFrom":makeQuery(id+"F3.opExtrude","CAP_FACE",FACE,{"disambiguationData":[OSD([subQ5,subQ1,subQ6,subQ7,subQ4,subQ3,subQ2,subQ0])],"isStart":false})})}),makeQuery(id+"F8.opExtrude","SWEPT_FACE",FACE,{"disambiguationData":[OSD([sQuery(id+"F7.wireOp",EDGE,"E67")])]})]});}
            var Q5;
            Q5=makeQuery(id+"F8.boolean.opBoolean","INTERSECT",EDGE,{"disambiguationData":[OD(0.0)],"derivedFrom":[makeQuery(id+"F5.opExtrude","SWEPT_FACE",FACE,{"disambiguationData":[OSD([sQuery(id+"F4.wireOp",EDGE,"E30")])]}),makeQuery(id+"F8.opExtrude","SWEPT_FACE",FACE,{"disambiguationData":[OSD([sQuery(id+"F7.wireOp",EDGE,"E67")])]})]});
            fillet(context, id + "F14", {"entities" : qUnion([Q0, Q1, Q2, Q3, Q4, Q5]), "radius" : 3 * mm, "tangentPropagation" : true, "allowEdgeOverflow" : false});
        }
        {
            var Q0;
            Q0=makeQuery(id+"F1.opExtrude","CAP_EDGE",EDGE,{"disambiguationData":[OSD([sQuery(id+"F0.wireOp",EDGE,"E1.bottom")])],"isStart":false});
            fillet(context, id + "F15", {"entities" : qUnion([Q0]), "radius" : 2 * mm, "tangentPropagation" : true, "allowEdgeOverflow" : false});
        }
        {
            var Q0;
            {var subQ0=sQuery(id+"F0.wireOp",EDGE,"E21.filletArc");var subQ1=sQuery(id+"F0.wireOp",EDGE,"E7");var subQ2=sQuery(id+"F0.wireOp",EDGE,"E6");var subQ3=sQuery(id+"F0.wireOp",EDGE,"E5");var subQ4=sQuery(id+"F0.wireOp",EDGE,"E4");var subQ5=sQuery(id+"F0.wireOp",EDGE,"E22.filletArc");var subQ6=sQuery(id+"F0.wireOp",EDGE,"E1.bottom");var subQ7=sQuery(id+"F0.wireOp",EDGE,"E1.right");var subQ8=sQuery(id+"F0.wireOp",EDGE,"E1.top");var subQ9=sQuery(id+"F0.wireOp",EDGE,"E1.left");var subQ10=sQuery(id+"F0.wireOp",EDGE,"E23.filletArc");var subQ11=sQuery(id+"F0.wireOp",EDGE,"E24.filletArc");Q0=makeQuery(id+"F2.boolean.opBoolean","SPLIT",FACE,{"disambiguationData":[TD([makeQuery(id+"F1.opExtrude","SWEPT_FACE",FACE,{"disambiguationData":[OSD([subQ6])]})])],"derivedFrom":makeQuery(id+"F1.opExtrude","CAP_FACE",FACE,{"disambiguationData":[OSD([subQ6,subQ8,subQ9,subQ7,subQ4,subQ3,subQ2,subQ1,subQ0,subQ5,subQ10,subQ11])],"isStart":true})});}
            var sketch = newSketch(context, id + "F16", { "sketchPlane" : qUnion([Q0])});
            skLineSegment(sketch, "E79", {"start": v(0, 74.25) * mm, "end": v(0, 104.25) * mm, "construction": true});
            skArc(sketch, "E80", {"start": v(15, 104.25) * mm, "mid": v(0, 119.25) * mm, "end": v(-15, 104.25) * mm});
            skLineSegment(sketch, "E81", {"start": v(15, 104.25) * mm, "end": v(15, 92.25) * mm});
            skLineSegment(sketch, "E82", {"start": v(-15, 104.25) * mm, "end": v(-15, 92.25) * mm});
            skLineSegment(sketch, "E83", {"start": v(-15, 92.25) * mm, "end": v(-33, 74.25) * mm});
            skLineSegment(sketch, "E84", {"start": v(15, 92.25) * mm, "end": v(33, 74.25) * mm});
            skCircle(sketch, "E85", {"center": v(0, 104.25) * mm, "radius": 6 * mm});
            skLineSegment(sketch, "E86", {"start": v(-74.25, 0) * mm, "end": v(74.25, 0) * mm, "construction": true});
            skLineSegment(sketch, "E87.MirrorCS", {"start": v(15, -104.25) * mm, "end": v(15, -92.25) * mm});
            skLineSegment(sketch, "E88.MirrorCS", {"start": v(-15, -104.25) * mm, "end": v(-15, -92.25) * mm});
            skLineSegment(sketch, "E89.MirrorCS", {"start": v(0, -74.25) * mm, "end": v(0, -104.25) * mm, "construction": true});
            skArc(sketch, "E90.MirrorCS", {"start": v(15, -104.25) * mm, "mid": v(0, -119.25) * mm, "end": v(-15, -104.25) * mm});
            skLineSegment(sketch, "E91.MirrorCS", {"start": v(-15, -92.25) * mm, "end": v(-33, -74.25) * mm});
            skLineSegment(sketch, "E92.MirrorCS", {"start": v(15, -92.25) * mm, "end": v(33, -74.25) * mm});
            skCircle(sketch, "E93.MirrorC", {"center": v(0, -104.25) * mm, "radius": 6 * mm});
            skSolve(sketch);
        }
        {
            var Q0;
            Q0=makeQuery(id+"F16.imprint","IMPRINT",FACE,{"disambiguationData":[TD([[makeQuery(id+"F16.imprint","IMPRINT",EDGE,{"derivedFrom":sQuery(id+"F16.wireOp",EDGE,"E80")}),1.0]])]});
            var Q1;
            Q1=makeQuery(id+"F16.imprint","IMPRINT",FACE,{"disambiguationData":[TD([[makeQuery(id+"F16.imprint","IMPRINT",EDGE,{"derivedFrom":makeQuery(id+"F1.opExtrude","CAP_EDGE",EDGE,{"disambiguationData":[OSD([sQuery(id+"F0.wireOp",EDGE,"E1.left")])],"isStart":true})}),-1.0]])]});
            var Q2;
            Q2=makeQuery(id+"F16.imprint","IMPRINT",FACE,{"disambiguationData":[TD([[makeQuery(id+"F16.imprint","IMPRINT",EDGE,{"derivedFrom":sQuery(id+"F16.wireOp",EDGE,"E87.MirrorCS")}),1.0]])]});
            var Q3;
            Q3=makeQuery(id+"F2.opExtrude","CAP_FACE",FACE,{"disambiguationData":[OSD([sQuery(id+"F0.wireOp",EDGE,"E12"),sQuery(id+"F0.wireOp",EDGE,"E13"),sQuery(id+"F0.wireOp",EDGE,"E14"),sQuery(id+"F0.wireOp",EDGE,"E15"),sQuery(id+"F0.wireOp",EDGE,"E17.filletArc"),sQuery(id+"F0.wireOp",EDGE,"E18.filletArc"),sQuery(id+"F0.wireOp",EDGE,"E19.filletArc"),sQuery(id+"F0.wireOp",EDGE,"E20.filletArc"),sQuery(id+"F0.wireOp",EDGE,"E25.0"),sQuery(id+"F0.wireOp",EDGE,"E25.1"),sQuery(id+"F0.wireOp",EDGE,"E25.2"),sQuery(id+"F0.wireOp",EDGE,"E25.3"),sQuery(id+"F0.wireOp",EDGE,"E25.4"),sQuery(id+"F0.wireOp",EDGE,"E25.5"),sQuery(id+"F0.wireOp",EDGE,"E25.6"),sQuery(id+"F0.wireOp",EDGE,"E25.7")])],"isStart":false});
            extrude(context, id + "F17", {"entities" : qUnion([Q0, Q1, Q2]), "endBound" : BoundingType.UP_TO_SURFACE, "endBoundEntityFace" : qUnion([Q3]), "depth" : 25 * mm});
        }
    });
